# Revit family: Domotics-DomesticRanges-GEWISS-SYSTEM_COMMAND-BLANKING_MODULE
name_source: partatom
category: Apparecchi elettrici
revit_build: Autodesk Revit 2016 (Build: 20161004_0715(x64)
units: mm (PartAtom-declared; Revit-internal decimal feet)

## family parameters
Condiviso = Sì
Host = Superficie
Mantenere orientamento annotazione = Sì
Punto di calcolo locali = Sì
Quota connettore circolare = Usa diametro
Taglio con vuoti quando caricato = Sì
Tipo di parte = Normale

## types (4) — shared parameters
Carico apparente = 0 VA
Catalogue = DOMOTICS
Catalogue Range = SYSTEM - Special plates
Electrocod = 0100
IDF = fd75645d-75fa-4554-9039-0c5bd0656d53
IDT = f96c9ae3-5101-45d8-b36f-9f18b0ca1788
Immagine tipo = GW21073.jpg
N. poli = 1
Produttore = GEWISS S.p.A.
Prospetto di default = 1219 mm
SEO = Blanking module
TIPO = System Copriforo_GENERICO : GW21073 Copriforo 2 moduli nero
Technical sheet = https://www.gewiss.com
URL = https://www.gewiss.com
Version file RFA = 19.4
Volt = 230 V

## per-type parameters (varying)
| type | Colour | Description: | Descrizione | EAN code | Modello | No. SYSTEM modules |
| GW21056 - BLANKING MODULE 1 GANG SY/BK | Black | 1 gang | BLANKING MODULE 1 GANG SY/BK | 8011564128217 | GW21056 | 1 |
| GW20073 - BLANKING MODULE 2 GANG SY/WT | White | 2 gang | BLANKING MODULE 2 GANG SY/WT | 8011564025943 | GW20073 | 2 |
| GW21073 - BLANKING MODULE 2 GANG SY/BK | Black | 2 gang | BLANKING MODULE 2 GANG SY/BK | 8011564128224 | GW21073 | 2 |
| GW20056 - BLANKING MODULE 1 GANG SY/WT | White | 1 gang | BLANKING MODULE 1 GANG SY/WT | 8011564001213 | GW20056 | 1 |

## geometry (parser evidence)
native form markers: Blend x2, Sweep x1
no freeform markers — native parametric forms only
